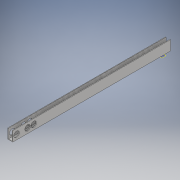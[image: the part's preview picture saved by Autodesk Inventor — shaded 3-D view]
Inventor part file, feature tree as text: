
AUTODESK INVENTOR PART (.ipt)
format: ipt  version: 2018 (Build 220112000, 112)  size: 140,288 bytes
history: native  units: in
note: dims shown in document units (in); Inventor stores cm internally (conversion verified against a paired STEP export)
features: sketch x4, extrude x4, plane x1
ambient origin geometry x8: Origin, YZ Plane, XZ Plane, XY Plane, X Axis, Y Axis, Z Axis, Center Point
bodies: Body1 (feature_tree)
feature tree (9):
  sketch  "Sketch1"  dims[d0=1.0in d1=32.0in]
  plane  "Work Plane3"
  extrude  "Extrusion3"  Depth=32.0in
  extrude  "Extrusion5"  Depth=0.125in TaperAngle=0.0deg
  extrude  "Extrusion6"  Depth=0.125in
  extrude  "Extrusion10"  Depth=2.0in TaperAngle=0.0deg
  sketch  "Sketch2"  dims[d2=0.125in d7=0.125in d8=0.0in]
  sketch  "Sketch4"  dims[d11=2.0in d12=0.0in d13=0.125in]
  sketch  "Sketch5"  dims[d14=0.125in d15=40.0in d16=0.0in d17=0.75in d18=1.0in d19=1.125in d22=2.25in d23=1.125in d26=1.25in d27=1.125in d30=2.0in d31=0.0in]
